# Revit family: Hager-MINIGAMMA-Surface_mounted-IP30-Without_Cover-With_DIN-Hosted-CH-it
name_source: partatom
category: Electrical Equipment
units: mm (PartAtom-declared; Revit-internal decimal feet)

## family parameters
Cut with Voids When Loaded = No
Host = Face
Maintain Annotation Orientation = Yes
Panel Configuration = Two Columns, Circuits Across
Part Type = Panelboard
Room Calculation Point = No
Round Connector Dimension = Use Diameter
Shared = No

## types (5) — shared parameters
BC_MODEL_ID = 1554389
BC_OBJECT_ID = 513896
BC_OBJECT_VERSION = #9
Code hager = ADD-EC000214_EU
EF000003 - modo di montaggio = apparente
EF000024 - resistente ai raggi UV = No
EF000049 - profondità = 82 mm  [stored 0.269029 ft]
EF000116 - numero RAL = 9010
EF000118 - con piastra di montaggio = No
EF000266 - numero di file = 1
EF001062 - versione EMC = No
EF001088 - possibilità di applicazione = No
EF001134 - barra DIN = Yes
EF005474 - grado di protezione (IP) = IP30
EF006244 - coperchio/porta trasparente = No
EF006306 - con serratura = No
EF015941 - porta di trasmissione del segnale = No
ETIM class code = EC000214
ETIM class name = Small distribution board
HG000001 - Numero di colonne = 1
HG000002-with door or cover-it = No
HG000003-Range-it = MINIGAMMA
HG000005-Thickness-it = 2 mm  [stored 0.00656168 ft]
HG000006-Flush mounted-it = No
HG000009-Double swing door-it = No
HG000010-Asymmetric doors-it = No
HG000011-Empty rows from bottom-it = No
HG000012-Door swing angle-it = 90.00°
HG000013-Door on the left-it = No
HG000014-Door on the right-it = Yes
HG000015-Clearance visibility-it = Yes
HG000016-Door 3D visibility-it = Yes
HG000017-Distance between poles-it = 18 mm  [stored 0.0590551 ft]
HG000060-RAL-number = 9010
HG000099-Onfly Template ID-it-CH = 507532
HGEF000266-Numero di file = 1
Manufacturer = Hager
Name = MINIGAMMA-Surface_mounted-IP30-Without_Cover-With_DIN-CH
Name BIM&CO = Electricity
Name hager = ADD_Enclosures_EC000214
Uniformat = Low Tension Service & Dist.
Uniformat code = D501001
zero-valued in all types: Default Elevation, EF000218 - profondità di montaggio, EF000332 - altezza di installazione, EF000846 - larghezza di montaggio, EF001131 - profondità interna, HG000007-Number of empty columns-it, HG000008-Number of empty rows-it

## per-type parameters (varying)
| type | BC_VARIANT_ID | EF000008 - larghezza | EF000040 - altezza | EF002950 - numero di unità modulari | EF015776 - morsetto di messa a terra | EF015777 - morsettiera a conduttore neutro | HG000004-Manufacturer reference-it | HGEF0002950-larghezza in unità di suddivisione |
| MINIGAMMA-Surface_mounted_W55_H160_D82_2_Modular_Spacing-GD102N | 1178995 | 55 mm  [stored 0.180446 ft] | 160 mm  [stored 0.524934 ft] | 2 | No | No | GD102N | 2 |
| MINIGAMMA-Surface_mounted_W110_H180_D82_4_Modular_Spacing-GD104N | 1178996 | 110 mm  [stored 0.360892 ft] | 180 mm  [stored 0.590551 ft] | 4 | Yes | Yes | GD104N | 4 |
| MINIGAMMA-Surface_mounted_W146_H180_D82_6_Modular_Spacing-GD106N | 1178997 | 146 mm  [stored 0.479003 ft] | 180 mm  [stored 0.590551 ft] | 6 | No | No | GD106N | 6 |
| MINIGAMMA-Surface_mounted_W182_H180_D82_8_Modular_Spacing-GD108N | 1178998 | 182 mm  [stored 0.597113 ft] | 180 mm  [stored 0.590551 ft] | 8 | No | No | GD108N | 8 |
| MINIGAMMA-Surface_mounted_W218_H180_D82_10_Modular_Spacing-GD110N | 1178999 | 218 mm  [stored 0.715223 ft] | 180 mm  [stored 0.590551 ft] | 10 | No | No | GD110N | 10 |

note: column(s) folded — value = type name in every type: Reference

note: [stored X ft] marks values corroborated as IEEE doubles in the binary element streams (Revit-internal decimal feet)

## geometry (parser evidence)
native form markers: Sweep x14
no freeform markers — native parametric forms only
